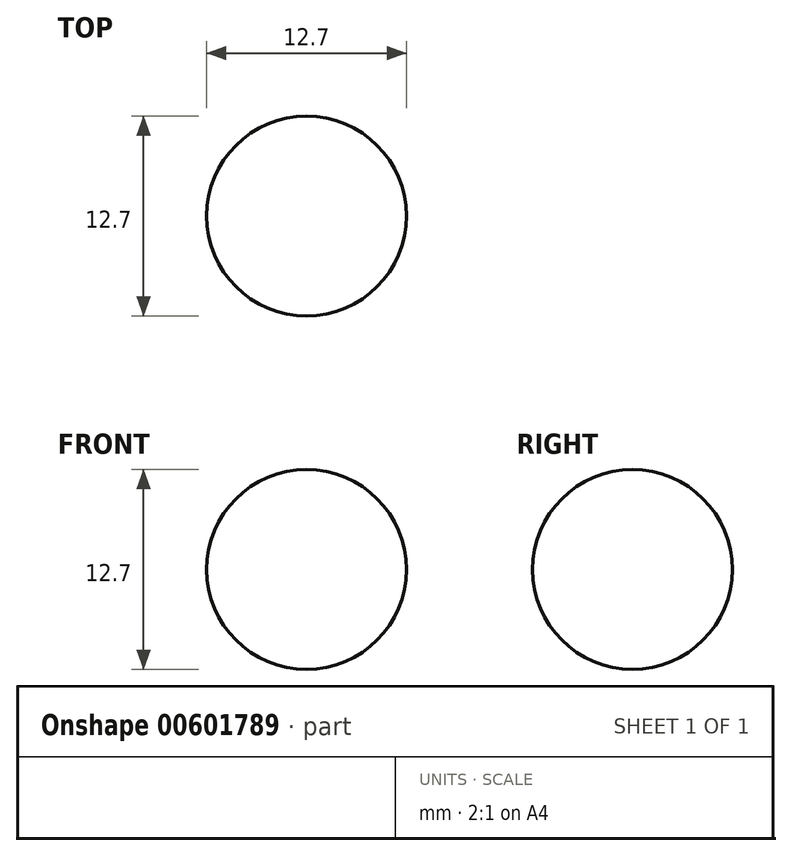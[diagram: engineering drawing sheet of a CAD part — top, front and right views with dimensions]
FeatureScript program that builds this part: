
annotation { "Feature Type Name" : "Feature", "Feature Type Description" : "" }
export const myFeature = defineFeature(function(context is Context, id is Id, definition is map)
    precondition{}
    {
        {
            var Q0;
            Q0=qCreatedBy(makeId("Front.planeOp"),FACE);
            var sketch = newSketch(context, id + "F0", { "sketchPlane" : qUnion([Q0])});
            skCircle(sketch, "E0", {"center": v(0, 0) * mm, "radius": 6.35 * mm});
            skLineSegment(sketch, "E1", {"start": v(0, 6.35) * mm, "end": v(0, -6.35) * mm});
            skSolve(sketch);
        }
        {
            var Q0;
            {var subQ0=sQuery(id+"F0.wireOp",EDGE,"E1");Q0=makeQuery(id+"F0.imprint","IMPRINT",FACE,{"disambiguationData":[TD([[makeQuery(id+"F0.imprint","IMPRINT",EDGE,{"derivedFrom":subQ0}),-1.0]])]});}
            var Q1;
            Q1=sQuery(id+"F0.wireOp",EDGE,"E1");
            revolve(context, id + "F1", {"entities" : qUnion([Q0]), "axis" : qUnion([Q1]), "revolveType" : RevolveType.FULL});
        }
    });
